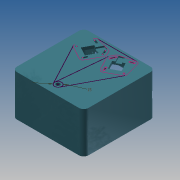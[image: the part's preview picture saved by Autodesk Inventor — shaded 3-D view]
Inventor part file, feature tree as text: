
AUTODESK INVENTOR PART (.ipt)
format: ipt  version: 2013 (Build 170138000, 138)  size: 638,976 bytes
history: native  units: mm
features: extrude x26, sketch x26, chamfer x4, reference x4, fillet x3, plane x3, mirror x2, projected_geometry x2, other x1
ambient origin geometry x8: Origin, YZ Plane, XZ Plane, XY Plane, X Axis, Y Axis, Z Axis, Center Point
bodies: Solid1 (feature_tree)
feature tree (71):
  extrude  "Extrusion1"  Depth=42.0mm
  fillet  "Fillet1"  Radius=31.0mm
  extrude  "Extrusion2"  Depth=5.5mm
  extrude  "Extrusion3"  Depth=3.5mm
  mirror  "Mirror1"
  sketch  "Sketch4"  dims[d8=5.5mm d9=5.5mm]
  extrude  "Extrusion4"  Depth=5.5mm
  extrude  "Extrusion22"  Depth=5.5mm
  extrude  "Extrusion23"  Depth=5.0mm TaperAngle=0.0deg
  fillet  "Fillet2"  Radius=15.0mm
  extrude  "Extrusion24"  Depth=8.5mm
  extrude  "Extrusion25"  Depth=5.0mm
  extrude  "Extrusion26"  Depth=10.0mm TaperAngle=0.0deg
  extrude  "Extrusion28"  Depth=5.0mm
  extrude  "Extrusion31"  Depth=12.5mm
  chamfer  "Chamfer2"  Distance=30.0mm
  sketch  "Sketch32"  dims[d121=1.0mm d122=2.0mm d123=45.0deg d124=3.0mm]
  plane  "Work Plane4"
  extrude  "Extrusion32"  Depth=8.0mm TaperAngle=0.0deg
  chamfer  "Chamfer3"  Distance=1.0mm
  extrude  "Extrusion33"  Depth=3.0mm
  extrude  "Extrusion34"  Depth=5.0mm
  sketch  "Sketch35"  dims[d141=0.5mm d142=8.6mm d143=0.0mm]
  extrude  "Extrusion35"  Depth=5.6mm TaperAngle=45.0deg
  extrude  "Extrusion36"  Depth=8.6mm TaperAngle=0.0deg
  extrude  "Extrusion37"  Depth=8.6mm TaperAngle=0.0deg
  extrude  "Extrusion38"  Depth=8.6mm TaperAngle=0.0deg
  extrude  "Extrusion39"  Depth=1.0mm
  mirror  "Mirror3"
  extrude  "Extrusion40"  Depth=8.6mm TaperAngle=0.0deg
  extrude  "Extrusion41"  Depth=42.96mm
  extrude  "Extrusion42"  Depth=8.0mm
  chamfer  "Chamfer4"  Distance=10.0mm
  fillet  "Fillet3"  Radius=10.0mm
  extrude  "Extrusion43"  Depth=36.0mm
  extrude  "Extrusion44"  Depth=3.0mm TaperAngle=0.0deg
  extrude  "Extrusion45"  Depth=15.0mm
  other  "Work Axis2"
  extrude  "Extrusion27"  Depth=3.0mm
  chamfer  "Chamfer1"  Distance=10.5mm
  sketch  "Sketch1"  dims[d0=198.0mm d2=42.0mm d3=31.0mm]
  sketch  "Sketch2"  dims[d4=5.5mm d5=5.5mm]
  sketch  "Sketch3"  dims[d6=5.0mm d7=3.5mm]
  projected_geometry  "Projected Loop1"
  sketch  "Sketch22"  dims[d10=6.0mm d11=0.0mm d12=5.5mm]
  sketch  "Sketch23"  dims[d13=5.0mm d14=0.0mm d15=5.0mm d16=0.0mm d17=15.0mm]
  sketch  "Sketch24"  dims[d19=5.0mm d20=0.0mm d100=8.5mm]
  sketch  "Sketch25"  dims[d102=10.0mm d103=0.0mm d104=5.0mm]
  sketch  "Sketch26"  dims[d105=150.0mm d106=10.0mm d107=0.0mm]
  plane  "Work Plane2"
  plane  "Work Plane3"
  sketch  "Sketch27"  dims[d108=10.0mm d109=5.0mm]
  sketch  "Sketch28"  dims[d110=75.0mm d111=0.0mm d112=12.5mm d114=30.0mm d115=0.0mm]
  sketch  "Sketch31"  dims[d116=13.0mm d117=8.0mm d118=0.0mm d119=1.0mm d120=0.0mm]
  reference  "Reference4"
  projected_geometry  "Projected Loop4"
  reference  "Reference5"
  sketch  "Sketch33"  dims[d126=3.0mm d127=0.0mm d135=5.0mm]
  reference  "Reference6"
  sketch  "Sketch34"  dims[d136=5.6mm d137=0.0mm d138=5.6mm d139=2.0mm d140=45.0deg]
  reference  "Reference7"
  sketch  "Sketch36"  dims[d144=8.6mm d145=2.0mm d146=45.0deg d147=8.6mm d148=0.0mm]
  sketch  "Sketch37"  dims[d149=3.0mm d150=8.6mm d151=0.0mm]
  sketch  "Sketch38"  dims[d152=1.0mm d153=1.0mm]
  sketch  "Sketch39"  dims[d154=8.6mm d155=0.0mm d156=8.6mm d157=0.0mm]
  sketch  "Sketch40"  dims[d158=88.88mm d160=42.96mm]
  sketch  "Sketch41"  dims[d161=3.0mm d162=8.0mm]
  sketch  "Sketch42"  dims[d163=40.0mm d164=10.0mm d165=0.0mm d166=10.0mm]
  sketch  "Sketch43"  dims[d169=5.0mm d170=36.0mm]
  sketch  "Sketch44"  dims[d171=3.0mm d172=0.0mm d173=3.0mm d174=0.0mm]
  sketch  "Sketch45"  dims[d175=12.0mm d177=15.0mm d178=3.0mm d179=10.5mm d180=4.0mm d181=0.0mm d182=8.0mm d184=4.0mm d185=0.0mm d187=3.1mm d188=0.0mm d189=2.0mm d190=2.0mm d191=45.0deg d192=2.0mm d193=3.5mm d195=100.0mm d196=5.0mm d197=3.1mm d198=0.0mm d199=6.0mm d201=3.0mm d202=0.0mm d203=3.0mm d204=0.0mm]
